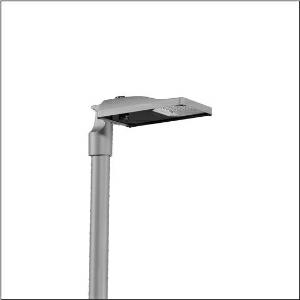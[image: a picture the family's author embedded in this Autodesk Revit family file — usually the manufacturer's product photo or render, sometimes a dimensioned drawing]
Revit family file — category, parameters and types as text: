
# Revit family: streetlight_sl_31_micro___st1_0a_5xh1d71t08ca_5556
name_source: partatom
category: Lighting Fixtures
units: mm (PartAtom-declared; Revit-internal decimal feet)

## family parameters
Cut with Voids When Loaded = No
Host = Face
Light Source = No
Part Type = Normal
Room Calculation Point = No
Round Connector Dimension = Use Diameter
Shared = No

## types (1)
- --- (1 x LED, 1170 lm, 10.2 W, 2200K)
    Apparent Load = 10 VA
    CIE Flux Codes = 37 72 97 100 100
    Color Rendering = 70
    Color Temperature = 2200K
    Default Elevation = 1800 mm
    Description = Streetlight SL 31 micro D4i, Desk-Remote mast luminaire for post-top, side-entry; light control with lens of PMMA; light distribution: ST1.0a, direct asymmetric distribution, for standard-compliant lighting for roads and squares; LED: luminous flux: 1.170lm, light colour: 722, colour temperature: 2200K; luminous efficacy: 114,7lm/W; control: pre-setting: logarithmic dimming characteristic, flexible luminous flux parameterisation, time-dependent luminous flux control, constant luminous flux control, power reduction, intelligent temperature release in ECG and LED module, overheat protection; luminaire housing, of diecast aluminium, SITECO metallic grey (DB 702S), corrosivity category C5 high according to DIN EN ISO 12944; cover of toughened safety glass, transparent, mast flange of diecast aluminium, SITECO metallic grey (DB 702S), spigot size: 76/60mm, mast flange included unmounted; cable length: 5,5m, connection cable pre-assembled; mains connection: 220..240V, AC, 50/60Hz; power consumption (at start of service life): 10,2W / (at end of service life): 10,5W / (with reduced operation 50%): 5,3W; protection rating (complete): IP66; insulation class (complete): insulation class II (safety insulation); impact resistance: IK09; certification: CE, ENEC, ENEC+, VDE, UKCA, ZD4i; permissible operating ambient temperature for outdoor applications: -40..+50°C; packaging unit: 1 piece

Light Distribution: ST1.0a
    Height = 76 mm
    Lamp = 1 x LED
    Lamp Light Flux = 1170 lm
    Lamp Power = 10.2 W
    Lamp count = 1
    Length = 467 mm
    Luminous efficacy = 115 lm/W
    Manufacturer = Siteco
    ModVariant = No
    Model = 5XH1D71T08CA
    Number of Poles = 1
    OnlyDefault = Yes
    Power Factor = 1
    Product Name = Streetlight SL 31 micro | ST1.0a
    Product group = mast luminaire | pylon top
    ProductGroupID = 6100
    Protection Class = Protection class II
    Protection Degree = IP 66
    RLX_Detail_Level = 1
    RLX_Emergency_Light_Flux = 0 lm
    RLX_Emergency_Type = 0
    RLX_Emergency_Type_DB = No
    RlxData = <blob elided: 23277 chars, md5=2b6bf040>
    Socket = socket
    Standby Power = 0 W
    System Light Flux = 1170 lm
    System Power = 10 W
    Type Comments = factory setting: luminous flux: 100 % | dim-lin: 254 | 386 mA
    Type Image = l_1300315.jpg
    URL = http://relux.com
    VarID = @adj_009553
    Voltage = 0 V
    Weight = 0.00 kg
    Width = 265 mm

## geometry (parser evidence)
native form markers: Blend x4, Sweep x11
no freeform markers — native parametric forms only
